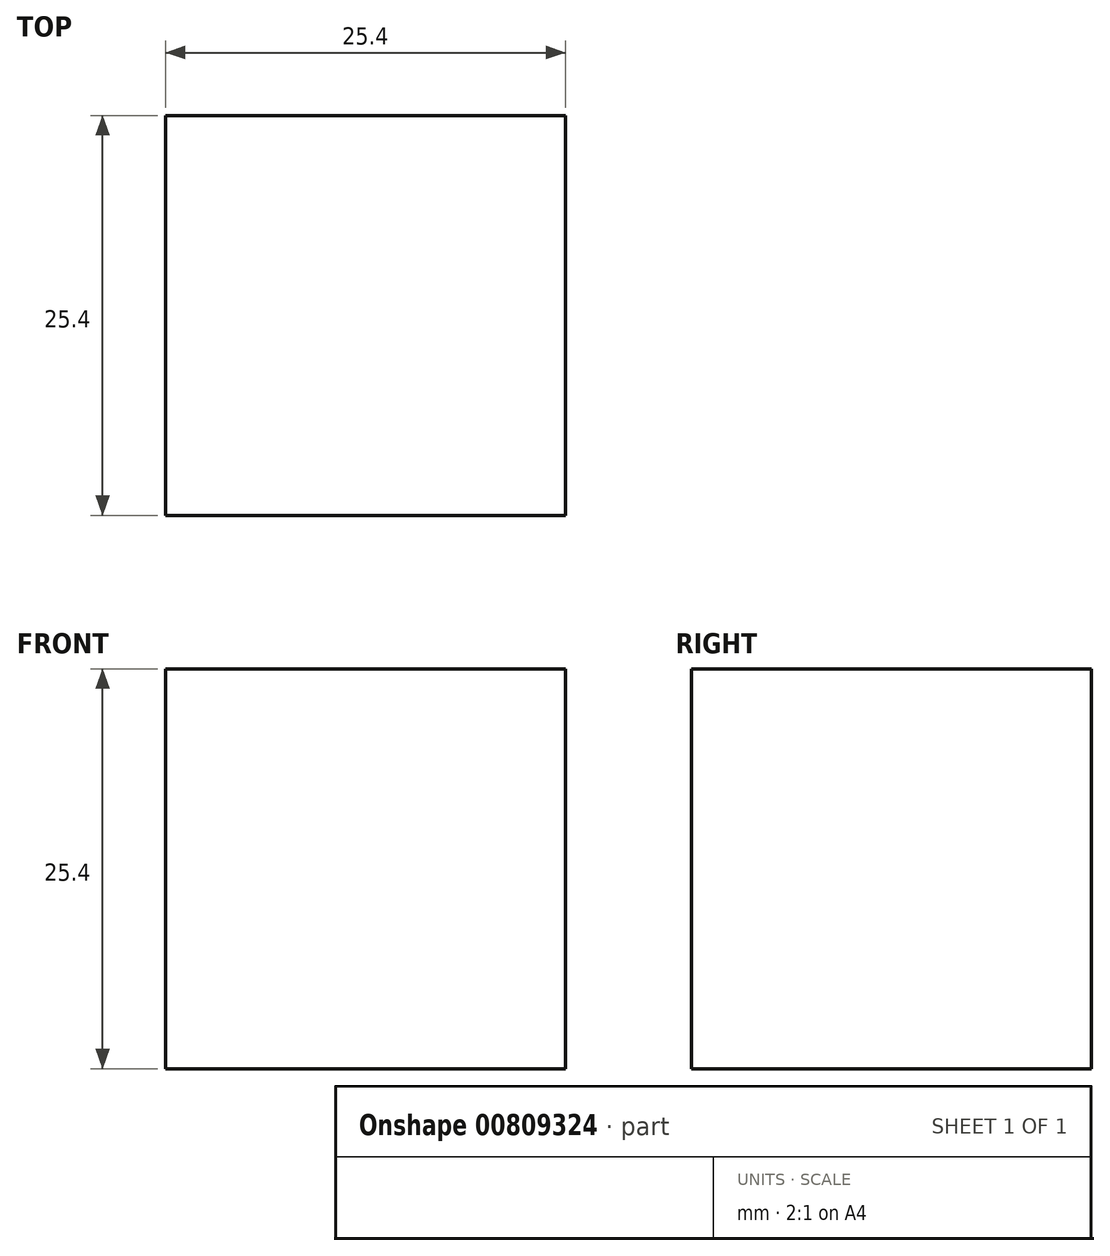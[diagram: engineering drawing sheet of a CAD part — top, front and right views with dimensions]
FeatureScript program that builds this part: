
annotation { "Feature Type Name" : "Feature", "Feature Type Description" : "" }
export const myFeature = defineFeature(function(context is Context, id is Id, definition is map)
    precondition{}
    {
        {
            var Q0;
            Q0=qCreatedBy(makeId("Top.planeOp"),FACE);
            var sketch = newSketch(context, id + "F0", { "sketchPlane" : qUnion([Q0])});
            skLineSegment(sketch, "E0.bottom", {"start": v(-49, 12.82) * mm, "end": v(-23.6, 12.82) * mm});
            skLineSegment(sketch, "E0.top", {"start": v(-49, -12.58) * mm, "end": v(-23.6, -12.58) * mm});
            skLineSegment(sketch, "E0.left", {"start": v(-49, 12.82) * mm, "end": v(-49, -12.58) * mm});
            skLineSegment(sketch, "E0.right", {"start": v(-23.6, 12.82) * mm, "end": v(-23.6, -12.58) * mm});
            skSolve(sketch);
        }
        {
            var Q0;
            Q0=makeQuery(id+"F0.imprint","IMPRINT",FACE,{"disambiguationData":[TD([[makeQuery(id+"F0.imprint","IMPRINT",EDGE,{"derivedFrom":sQuery(id+"F0.wireOp",EDGE,"E0.bottom")}),-1.0]])]});
            extrude(context, id + "F1", {"entities" : qUnion([Q0]), "depth" : 25.4 * mm, "offsetDistance" : 25.4 * mm});
        }
    });
